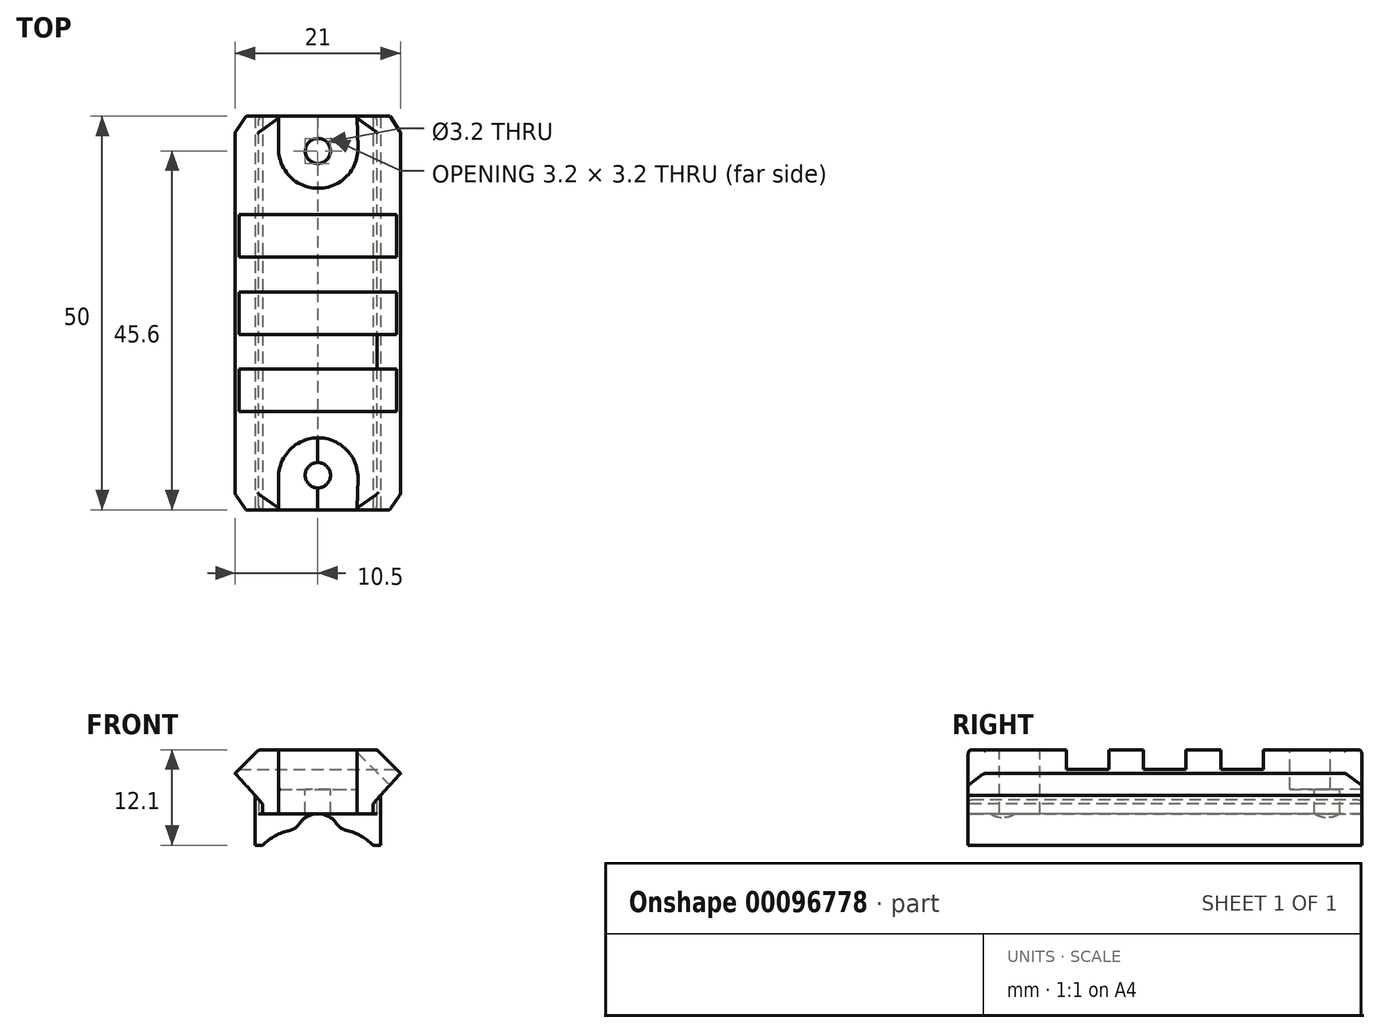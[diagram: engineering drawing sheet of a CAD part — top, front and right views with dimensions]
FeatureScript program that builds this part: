
annotation { "Feature Type Name" : "Feature", "Feature Type Description" : "" }
export const myFeature = defineFeature(function(context is Context, id is Id, definition is map)
    precondition{}
    {
        {
            var Q0;
            Q0=qCreatedBy(makeId("Front.planeOp"),FACE);
            var sketch = newSketch(context, id + "F0", { "sketchPlane" : qUnion([Q0])});
            skPoint(sketch, "E0", {"position": v(7.5, 0) * mm});
            skPoint(sketch, "E1", {"position": v(-7.5, 0) * mm});
            skPoint(sketch, "E2", {"position": v(0, 3.3) * mm});
            skPoint(sketch, "E3", {"position": v(0, -4.8) * mm});
            skLineSegment(sketch, "E4", {"start": v(7.5, -4.8) * mm, "end": v(-7.5, -4.8) * mm});
            skLineSegment(sketch, "E5", {"start": v(7.5, -4.8) * mm, "end": v(7.5, -3) * mm});
            skLineSegment(sketch, "E6", {"start": v(-7.5, -3) * mm, "end": v(-7.5, -4.8) * mm});
            skLineSegment(sketch, "E7", {"start": v(-7.5, -3) * mm, "end": v(-10.5, 0.3) * mm});
            skLineSegment(sketch, "E8", {"start": v(7.5, -3) * mm, "end": v(10.5, 0.3) * mm});
            skPoint(sketch, "E9", {"position": v(7.5, 3.3) * mm});
            skPoint(sketch, "E10", {"position": v(-7.5, 3.3) * mm});
            skLineSegment(sketch, "E11", {"start": v(-10.5, 0.3) * mm, "end": v(-7.5, 3.3) * mm});
            skLineSegment(sketch, "E12", {"start": v(10.5, 0.3) * mm, "end": v(7.5, 3.3) * mm});
            skLineSegment(sketch, "E13", {"start": v(-7.5, 3.3) * mm, "end": v(7.5, 3.3) * mm});
            skSolve(sketch);
        }
        {
            var Q0;
            Q0 = qSketchRegion(id + "F0", true);
            extrude(context, id + "F1", {"entities" : qUnion([Q0]), "endBound" : BoundingType.SYMMETRIC, "depth" : 50 * mm});
        }
        {
            var Q0;
            Q0=makeQuery(id+"F1.opExtrude","SWEPT_FACE",FACE,{"disambiguationData":[OSD([sQuery(id+"F0.wireOp",EDGE,"E13")])]});
            var sketch = newSketch(context, id + "F2", { "sketchPlane" : qUnion([Q0])});
            skPoint(sketch, "E14", {"position": v(0, 2.7) * mm});
            skPoint(sketch, "E15", {"position": v(0, -2.7) * mm});
            skLineSegment(sketch, "E16", {"start": v(-14, -2.7) * mm, "end": v(14, -2.7) * mm});
            skLineSegment(sketch, "E17", {"start": v(14, -2.7) * mm, "end": v(14, 2.7) * mm});
            skLineSegment(sketch, "E18", {"start": v(14, 2.7) * mm, "end": v(-14, 2.7) * mm});
            skLineSegment(sketch, "E19", {"start": v(-14, -2.7) * mm, "end": v(-14, 2.7) * mm});
            skLineSegment(sketch, "E20", {"start": v(0, 25) * mm, "end": v(0, 10) * mm});
            skLineSegment(sketch, "E21.0.1.0", {"start": v(-14, 7.12) * mm, "end": v(-14.1, 12.52) * mm});
            skLineSegment(sketch, "E21.0.1.1", {"start": v(14.12, 12.52) * mm, "end": v(-14.1, 12.52) * mm});
            skLineSegment(sketch, "E21.0.1.2", {"start": v(-14, 7.12) * mm, "end": v(14.12, 7.12) * mm});
            skLineSegment(sketch, "E21.0.1.3", {"start": v(14.12, 7.12) * mm, "end": v(14.12, 12.52) * mm});
            skLineSegment(sketch, "E21.direction2", {"start": v(-14, -2.7) * mm, "end": v(-14, 7.12) * mm, "construction": true});
            skLineSegment(sketch, "E22.0.1.0", {"start": v(-13.9, -12.52) * mm, "end": v(14.62, -12.52) * mm});
            skLineSegment(sketch, "E22.0.1.1", {"start": v(-13.9, -12.52) * mm, "end": v(-13.9, -7.12) * mm});
            skLineSegment(sketch, "E22.0.1.2", {"start": v(14.62, -7.12) * mm, "end": v(-13.9, -7.12) * mm});
            skLineSegment(sketch, "E22.0.1.3", {"start": v(14.62, -12.52) * mm, "end": v(14.62, -7.12) * mm});
            skLineSegment(sketch, "E22.direction2", {"start": v(-14, -2.7) * mm, "end": v(-13.9, -12.52) * mm, "construction": true});
            skLineSegment(sketch, "E23", {"start": v(0, -7.12) * mm, "end": v(0, -12.52) * mm});
            skSolve(sketch);
        }
        {
            var Q0;
            Q0 = qSketchRegion(id + "F2", true);
            extrude(context, id + "F3", {"entities" : qUnion([Q0]), "operationType" : NewBodyOperationType.REMOVE, "oppositeDirection" : true, "depth" : 2.5 * mm});
        }
        {
            var Q0;
            Q0=makeQuery(id+"F1.opExtrude","CAP_EDGE",EDGE,{"disambiguationData":[OSD([sQuery(id+"F0.wireOp",EDGE,"E12")])],"isStart":true});
            var Q1;
            Q1=makeQuery(id+"F1.opExtrude","CAP_EDGE",EDGE,{"disambiguationData":[OSD([sQuery(id+"F0.wireOp",EDGE,"E11")])],"isStart":true});
            var Q2;
            Q2=makeQuery(id+"F1.opExtrude","CAP_EDGE",EDGE,{"disambiguationData":[OSD([sQuery(id+"F0.wireOp",EDGE,"E12")])],"isStart":false});
            var Q3;
            Q3=makeQuery(id+"F1.opExtrude","CAP_EDGE",EDGE,{"disambiguationData":[OSD([sQuery(id+"F0.wireOp",EDGE,"E11")])],"isStart":false});
            chamfer(context, id + "F4", {"entities" : qUnion([Q0, Q1, Q2, Q3]), "width" : 2 * mm, "tangentPropagation" : true});
        }
        {
            var Q0;
            {var subQ0=sQuery(id+"F0.wireOp",EDGE,"E11");var subQ1=sQuery(id+"F0.wireOp",EDGE,"E13");Q0=makeQuery(id+"F3.boolean.opBoolean","SPLIT",EDGE,{"disambiguationData":[TD([makeQuery(id+"F3.opExtrude","SWEPT_FACE",FACE,{"disambiguationData":[OSD([sQuery(id+"F2.wireOp",EDGE,"E21.0.2.1")])]})])],"derivedFrom":makeQuery(id+"F1.opExtrude","SWEPT_EDGE",EDGE,{"disambiguationData":[OSD([subQ0,subQ1])]})});}
            var Q1;
            {var subQ0=sQuery(id+"F0.wireOp",EDGE,"E11");var subQ1=sQuery(id+"F0.wireOp",EDGE,"E13");Q1=makeQuery(id+"F3.boolean.opBoolean","SPLIT",EDGE,{"disambiguationData":[TD([makeQuery(id+"F3.opExtrude","SWEPT_FACE",FACE,{"disambiguationData":[OSD([sQuery(id+"F2.wireOp",EDGE,"E21.0.1.1")])]})])],"derivedFrom":makeQuery(id+"F1.opExtrude","SWEPT_EDGE",EDGE,{"disambiguationData":[OSD([subQ0,subQ1])]})});}
            var Q2;
            {var subQ0=sQuery(id+"F0.wireOp",EDGE,"E11");var subQ1=sQuery(id+"F0.wireOp",EDGE,"E13");Q2=makeQuery(id+"F3.boolean.opBoolean","SPLIT",EDGE,{"disambiguationData":[TD([makeQuery(id+"F3.opExtrude","SWEPT_FACE",FACE,{"disambiguationData":[OSD([sQuery(id+"F2.wireOp",EDGE,"E18")])]})])],"derivedFrom":makeQuery(id+"F1.opExtrude","SWEPT_EDGE",EDGE,{"disambiguationData":[OSD([subQ0,subQ1])]})});}
            var Q3;
            {var subQ0=sQuery(id+"F0.wireOp",EDGE,"E11");var subQ1=sQuery(id+"F0.wireOp",EDGE,"E13");Q3=makeQuery(id+"F3.boolean.opBoolean","SPLIT",EDGE,{"disambiguationData":[TD([makeQuery(id+"F3.opExtrude","SWEPT_FACE",FACE,{"disambiguationData":[OSD([sQuery(id+"F2.wireOp",EDGE,"E16")])]})])],"derivedFrom":makeQuery(id+"F1.opExtrude","SWEPT_EDGE",EDGE,{"disambiguationData":[OSD([subQ0,subQ1])]})});}
            var Q4;
            {var subQ0=sQuery(id+"F0.wireOp",EDGE,"E11");var subQ1=sQuery(id+"F0.wireOp",EDGE,"E13");Q4=makeQuery(id+"F3.boolean.opBoolean","SPLIT",EDGE,{"disambiguationData":[TD([makeQuery(id+"F3.opExtrude","SWEPT_FACE",FACE,{"disambiguationData":[OSD([sQuery(id+"F2.wireOp",EDGE,"E22.0.1.0")])]})])],"derivedFrom":makeQuery(id+"F1.opExtrude","SWEPT_EDGE",EDGE,{"disambiguationData":[OSD([subQ0,subQ1])]})});}
            var Q5;
            {var subQ0=sQuery(id+"F0.wireOp",EDGE,"E11");var subQ1=sQuery(id+"F0.wireOp",EDGE,"E13");Q5=makeQuery(id+"F3.boolean.opBoolean","SPLIT",EDGE,{"disambiguationData":[TD([makeQuery(id+"F3.opExtrude","SWEPT_FACE",FACE,{"disambiguationData":[OSD([sQuery(id+"F2.wireOp",EDGE,"E22.0.2.0")])]})])],"derivedFrom":makeQuery(id+"F1.opExtrude","SWEPT_EDGE",EDGE,{"disambiguationData":[OSD([subQ0,subQ1])]})});}
            var Q6;
            {var subQ0=sQuery(id+"F0.wireOp",EDGE,"E12");var subQ1=sQuery(id+"F0.wireOp",EDGE,"E13");Q6=makeQuery(id+"F3.boolean.opBoolean","SPLIT",EDGE,{"disambiguationData":[TD([makeQuery(id+"F3.opExtrude","SWEPT_FACE",FACE,{"disambiguationData":[OSD([sQuery(id+"F2.wireOp",EDGE,"E22.0.2.0")])]})])],"derivedFrom":makeQuery(id+"F1.opExtrude","SWEPT_EDGE",EDGE,{"disambiguationData":[OSD([subQ0,subQ1])]})});}
            var Q7;
            {var subQ0=sQuery(id+"F0.wireOp",EDGE,"E12");var subQ1=sQuery(id+"F0.wireOp",EDGE,"E13");Q7=makeQuery(id+"F3.boolean.opBoolean","SPLIT",EDGE,{"disambiguationData":[TD([makeQuery(id+"F3.opExtrude","SWEPT_FACE",FACE,{"disambiguationData":[OSD([sQuery(id+"F2.wireOp",EDGE,"E22.0.1.0")])]})])],"derivedFrom":makeQuery(id+"F1.opExtrude","SWEPT_EDGE",EDGE,{"disambiguationData":[OSD([subQ0,subQ1])]})});}
            var Q8;
            {var subQ0=sQuery(id+"F0.wireOp",EDGE,"E12");var subQ1=sQuery(id+"F0.wireOp",EDGE,"E13");Q8=makeQuery(id+"F3.boolean.opBoolean","SPLIT",EDGE,{"disambiguationData":[TD([makeQuery(id+"F3.opExtrude","SWEPT_FACE",FACE,{"disambiguationData":[OSD([sQuery(id+"F2.wireOp",EDGE,"E18")])]})])],"derivedFrom":makeQuery(id+"F1.opExtrude","SWEPT_EDGE",EDGE,{"disambiguationData":[OSD([subQ0,subQ1])]})});}
            var Q9;
            {var subQ0=sQuery(id+"F0.wireOp",EDGE,"E12");var subQ1=sQuery(id+"F0.wireOp",EDGE,"E13");Q9=makeQuery(id+"F3.boolean.opBoolean","SPLIT",EDGE,{"disambiguationData":[TD([makeQuery(id+"F3.opExtrude","SWEPT_FACE",FACE,{"disambiguationData":[OSD([sQuery(id+"F2.wireOp",EDGE,"E21.0.1.1")])]})])],"derivedFrom":makeQuery(id+"F1.opExtrude","SWEPT_EDGE",EDGE,{"disambiguationData":[OSD([subQ0,subQ1])]})});}
            var Q10;
            {var subQ0=sQuery(id+"F0.wireOp",EDGE,"E12");var subQ1=sQuery(id+"F0.wireOp",EDGE,"E13");Q10=makeQuery(id+"F3.boolean.opBoolean","SPLIT",EDGE,{"disambiguationData":[TD([makeQuery(id+"F3.opExtrude","SWEPT_FACE",FACE,{"disambiguationData":[OSD([sQuery(id+"F2.wireOp",EDGE,"E21.0.2.1")])]})])],"derivedFrom":makeQuery(id+"F1.opExtrude","SWEPT_EDGE",EDGE,{"disambiguationData":[OSD([subQ0,subQ1])]})});}
            var Q11;
            {var subQ0=sQuery(id+"F0.wireOp",EDGE,"E13");var subQ2=sQuery(id+"F0.wireOp",EDGE,"E11");Q11=makeQuery(id+"F4.opChamfer","BLEND_EDGE",EDGE,{"blendedFrom":[makeQuery(id+"F1.opExtrude","CAP_EDGE",EDGE,{"disambiguationData":[OSD([subQ2])],"isStart":true}),makeQuery(id+"F3.boolean.opBoolean","SPLIT",FACE,{"disambiguationData":[TD([makeQuery(id+"F3.opExtrude","SWEPT_FACE",FACE,{"disambiguationData":[OSD([sQuery(id+"F2.wireOp",EDGE,"E21.0.3.1")])]})])],"derivedFrom":makeQuery(id+"F1.opExtrude","SWEPT_FACE",FACE,{"disambiguationData":[OSD([subQ0])]})})],"blendedInto":[makeQuery(id+"F3.boolean.opBoolean","SPLIT",FACE,{"disambiguationData":[TD([makeQuery(id+"F3.opExtrude","SWEPT_FACE",FACE,{"disambiguationData":[OSD([sQuery(id+"F2.wireOp",EDGE,"E21.0.3.1")])]})])],"derivedFrom":makeQuery(id+"F1.opExtrude","SWEPT_FACE",FACE,{"disambiguationData":[OSD([subQ0])]})})]});}
            var Q12;
            {var subQ0=sQuery(id+"F0.wireOp",EDGE,"E11");Q12=makeQuery(id+"F4.opChamfer","BLEND_EDGE",EDGE,{"blendedFrom":[makeQuery(id+"F1.opExtrude","CAP_EDGE",EDGE,{"disambiguationData":[OSD([subQ0])],"isStart":true}),makeQuery(id+"F1.opExtrude","CAP_FACE",FACE,{"disambiguationData":[OSD([sQuery(id+"F0.wireOp",EDGE,"E4"),sQuery(id+"F0.wireOp",EDGE,"E5"),sQuery(id+"F0.wireOp",EDGE,"E6"),sQuery(id+"F0.wireOp",EDGE,"E7"),sQuery(id+"F0.wireOp",EDGE,"E8"),subQ0,sQuery(id+"F0.wireOp",EDGE,"E12"),sQuery(id+"F0.wireOp",EDGE,"E13")])],"isStart":true})],"blendedInto":[makeQuery(id+"F1.opExtrude","CAP_FACE",FACE,{"disambiguationData":[OSD([sQuery(id+"F0.wireOp",EDGE,"E4"),sQuery(id+"F0.wireOp",EDGE,"E5"),sQuery(id+"F0.wireOp",EDGE,"E6"),sQuery(id+"F0.wireOp",EDGE,"E7"),sQuery(id+"F0.wireOp",EDGE,"E8"),subQ0,sQuery(id+"F0.wireOp",EDGE,"E12"),sQuery(id+"F0.wireOp",EDGE,"E13")])],"isStart":true})]});}
            var Q13;
            {var subQ0=sQuery(id+"F0.wireOp",EDGE,"E13");var subQ1=sQuery(id+"F0.wireOp",EDGE,"E12");Q13=makeQuery(id+"F4.opChamfer","BLEND_EDGE",EDGE,{"blendedFrom":[makeQuery(id+"F1.opExtrude","CAP_EDGE",EDGE,{"disambiguationData":[OSD([subQ1])],"isStart":true}),makeQuery(id+"F3.boolean.opBoolean","SPLIT",FACE,{"disambiguationData":[TD([makeQuery(id+"F3.opExtrude","SWEPT_FACE",FACE,{"disambiguationData":[OSD([sQuery(id+"F2.wireOp",EDGE,"E21.0.3.1")])]})])],"derivedFrom":makeQuery(id+"F1.opExtrude","SWEPT_FACE",FACE,{"disambiguationData":[OSD([subQ0])]})})],"blendedInto":[makeQuery(id+"F3.boolean.opBoolean","SPLIT",FACE,{"disambiguationData":[TD([makeQuery(id+"F3.opExtrude","SWEPT_FACE",FACE,{"disambiguationData":[OSD([sQuery(id+"F2.wireOp",EDGE,"E21.0.3.1")])]})])],"derivedFrom":makeQuery(id+"F1.opExtrude","SWEPT_FACE",FACE,{"disambiguationData":[OSD([subQ0])]})})]});}
            var Q14;
            {var subQ0=sQuery(id+"F0.wireOp",EDGE,"E12");Q14=makeQuery(id+"F4.opChamfer","BLEND_EDGE",EDGE,{"blendedFrom":[makeQuery(id+"F1.opExtrude","CAP_EDGE",EDGE,{"disambiguationData":[OSD([subQ0])],"isStart":true}),makeQuery(id+"F1.opExtrude","SWEPT_FACE",FACE,{"disambiguationData":[OSD([subQ0])]})],"blendedInto":[makeQuery(id+"F1.opExtrude","SWEPT_FACE",FACE,{"disambiguationData":[OSD([subQ0])]})]});}
            var Q15;
            {var subQ0=sQuery(id+"F0.wireOp",EDGE,"E11");Q15=makeQuery(id+"F4.opChamfer","BLEND_EDGE",EDGE,{"blendedFrom":[makeQuery(id+"F1.opExtrude","CAP_EDGE",EDGE,{"disambiguationData":[OSD([subQ0])],"isStart":true}),makeQuery(id+"F1.opExtrude","SWEPT_FACE",FACE,{"disambiguationData":[OSD([subQ0])]})],"blendedInto":[makeQuery(id+"F1.opExtrude","SWEPT_FACE",FACE,{"disambiguationData":[OSD([subQ0])]})]});}
            var Q16;
            {var subQ0=sQuery(id+"F0.wireOp",EDGE,"E12");Q16=makeQuery(id+"F4.opChamfer","BLEND_EDGE",EDGE,{"blendedFrom":[makeQuery(id+"F1.opExtrude","CAP_EDGE",EDGE,{"disambiguationData":[OSD([subQ0])],"isStart":false}),makeQuery(id+"F1.opExtrude","CAP_FACE",FACE,{"disambiguationData":[OSD([sQuery(id+"F0.wireOp",EDGE,"E4"),sQuery(id+"F0.wireOp",EDGE,"E5"),sQuery(id+"F0.wireOp",EDGE,"E6"),sQuery(id+"F0.wireOp",EDGE,"E7"),sQuery(id+"F0.wireOp",EDGE,"E8"),sQuery(id+"F0.wireOp",EDGE,"E11"),subQ0,sQuery(id+"F0.wireOp",EDGE,"E13")])],"isStart":false})],"blendedInto":[makeQuery(id+"F1.opExtrude","CAP_FACE",FACE,{"disambiguationData":[OSD([sQuery(id+"F0.wireOp",EDGE,"E4"),sQuery(id+"F0.wireOp",EDGE,"E5"),sQuery(id+"F0.wireOp",EDGE,"E6"),sQuery(id+"F0.wireOp",EDGE,"E7"),sQuery(id+"F0.wireOp",EDGE,"E8"),sQuery(id+"F0.wireOp",EDGE,"E11"),subQ0,sQuery(id+"F0.wireOp",EDGE,"E13")])],"isStart":false})]});}
            var Q17;
            {var subQ0=sQuery(id+"F0.wireOp",EDGE,"E12");Q17=makeQuery(id+"F4.opChamfer","BLEND_EDGE",EDGE,{"blendedFrom":[makeQuery(id+"F1.opExtrude","CAP_EDGE",EDGE,{"disambiguationData":[OSD([subQ0])],"isStart":false}),makeQuery(id+"F1.opExtrude","SWEPT_FACE",FACE,{"disambiguationData":[OSD([subQ0])]})],"blendedInto":[makeQuery(id+"F1.opExtrude","SWEPT_FACE",FACE,{"disambiguationData":[OSD([subQ0])]})]});}
            var Q18;
            {var subQ0=sQuery(id+"F0.wireOp",EDGE,"E13");var subQ1=sQuery(id+"F0.wireOp",EDGE,"E12");Q18=makeQuery(id+"F4.opChamfer","BLEND_EDGE",EDGE,{"blendedFrom":[makeQuery(id+"F1.opExtrude","CAP_EDGE",EDGE,{"disambiguationData":[OSD([subQ1])],"isStart":false}),makeQuery(id+"F3.boolean.opBoolean","SPLIT",FACE,{"disambiguationData":[TD([makeQuery(id+"F3.opExtrude","SWEPT_FACE",FACE,{"disambiguationData":[OSD([sQuery(id+"F2.wireOp",EDGE,"E22.0.3.0")])]})])],"derivedFrom":makeQuery(id+"F1.opExtrude","SWEPT_FACE",FACE,{"disambiguationData":[OSD([subQ0])]})})],"blendedInto":[makeQuery(id+"F3.boolean.opBoolean","SPLIT",FACE,{"disambiguationData":[TD([makeQuery(id+"F3.opExtrude","SWEPT_FACE",FACE,{"disambiguationData":[OSD([sQuery(id+"F2.wireOp",EDGE,"E22.0.3.0")])]})])],"derivedFrom":makeQuery(id+"F1.opExtrude","SWEPT_FACE",FACE,{"disambiguationData":[OSD([subQ0])]})})]});}
            var Q19;
            {var subQ0=sQuery(id+"F0.wireOp",EDGE,"E11");Q19=makeQuery(id+"F4.opChamfer","BLEND_EDGE",EDGE,{"blendedFrom":[makeQuery(id+"F1.opExtrude","CAP_EDGE",EDGE,{"disambiguationData":[OSD([subQ0])],"isStart":false}),makeQuery(id+"F1.opExtrude","CAP_FACE",FACE,{"disambiguationData":[OSD([sQuery(id+"F0.wireOp",EDGE,"E4"),sQuery(id+"F0.wireOp",EDGE,"E5"),sQuery(id+"F0.wireOp",EDGE,"E6"),sQuery(id+"F0.wireOp",EDGE,"E7"),sQuery(id+"F0.wireOp",EDGE,"E8"),subQ0,sQuery(id+"F0.wireOp",EDGE,"E12"),sQuery(id+"F0.wireOp",EDGE,"E13")])],"isStart":false})],"blendedInto":[makeQuery(id+"F1.opExtrude","CAP_FACE",FACE,{"disambiguationData":[OSD([sQuery(id+"F0.wireOp",EDGE,"E4"),sQuery(id+"F0.wireOp",EDGE,"E5"),sQuery(id+"F0.wireOp",EDGE,"E6"),sQuery(id+"F0.wireOp",EDGE,"E7"),sQuery(id+"F0.wireOp",EDGE,"E8"),subQ0,sQuery(id+"F0.wireOp",EDGE,"E12"),sQuery(id+"F0.wireOp",EDGE,"E13")])],"isStart":false})]});}
            var Q20;
            {var subQ0=sQuery(id+"F0.wireOp",EDGE,"E13");var subQ2=sQuery(id+"F0.wireOp",EDGE,"E11");Q20=makeQuery(id+"F4.opChamfer","BLEND_EDGE",EDGE,{"blendedFrom":[makeQuery(id+"F1.opExtrude","CAP_EDGE",EDGE,{"disambiguationData":[OSD([subQ2])],"isStart":false}),makeQuery(id+"F3.boolean.opBoolean","SPLIT",FACE,{"disambiguationData":[TD([makeQuery(id+"F3.opExtrude","SWEPT_FACE",FACE,{"disambiguationData":[OSD([sQuery(id+"F2.wireOp",EDGE,"E22.0.3.0")])]})])],"derivedFrom":makeQuery(id+"F1.opExtrude","SWEPT_FACE",FACE,{"disambiguationData":[OSD([subQ0])]})})],"blendedInto":[makeQuery(id+"F3.boolean.opBoolean","SPLIT",FACE,{"disambiguationData":[TD([makeQuery(id+"F3.opExtrude","SWEPT_FACE",FACE,{"disambiguationData":[OSD([sQuery(id+"F2.wireOp",EDGE,"E22.0.3.0")])]})])],"derivedFrom":makeQuery(id+"F1.opExtrude","SWEPT_FACE",FACE,{"disambiguationData":[OSD([subQ0])]})})]});}
            var Q21;
            {var subQ0=sQuery(id+"F0.wireOp",EDGE,"E11");Q21=makeQuery(id+"F4.opChamfer","BLEND_EDGE",EDGE,{"blendedFrom":[makeQuery(id+"F1.opExtrude","CAP_EDGE",EDGE,{"disambiguationData":[OSD([subQ0])],"isStart":false}),makeQuery(id+"F1.opExtrude","SWEPT_FACE",FACE,{"disambiguationData":[OSD([subQ0])]})],"blendedInto":[makeQuery(id+"F1.opExtrude","SWEPT_FACE",FACE,{"disambiguationData":[OSD([subQ0])]})]});}
            var Q22;
            Q22=makeQuery(id+"F1.opExtrude","CAP_EDGE",EDGE,{"disambiguationData":[OSD([sQuery(id+"F0.wireOp",EDGE,"E6")])],"isStart":false});
            var Q23;
            Q23=makeQuery(id+"F1.opExtrude","CAP_EDGE",EDGE,{"disambiguationData":[OSD([sQuery(id+"F0.wireOp",EDGE,"E5")])],"isStart":false});
            var Q24;
            Q24=makeQuery(id+"F1.opExtrude","CAP_EDGE",EDGE,{"disambiguationData":[OSD([sQuery(id+"F0.wireOp",EDGE,"E5")])],"isStart":true});
            var Q25;
            Q25=makeQuery(id+"F1.opExtrude","CAP_EDGE",EDGE,{"disambiguationData":[OSD([sQuery(id+"F0.wireOp",EDGE,"E6")])],"isStart":true});
            fillet(context, id + "F5", {"entities" : qUnion([Q0, Q1, Q2, Q3, Q4, Q5, Q6, Q7, Q8, Q9, Q10, Q11, Q12, Q13, Q14, Q15, Q16, Q17, Q18, Q19, Q20, Q21, Q22, Q23, Q24, Q25]), "radius" : 0.5 * mm, "tangentPropagation" : true, "allowEdgeOverflow" : false});
        }
        {
            var Q0;
            Q0=qCreatedBy(makeId("Right.planeOp"),FACE);
            var sketch = newSketch(context, id + "F6", { "sketchPlane" : qUnion([Q0])});
            skLineSegment(sketch, "E24.bottom", {"start": v(-60.58, 29.92) * mm, "end": v(-11.98, 29.92) * mm});
            skLineSegment(sketch, "E24.top", {"start": v(-60.58, -17.9) * mm, "end": v(-11.98, -17.9) * mm});
            skLineSegment(sketch, "E24.left", {"start": v(-60.58, 29.92) * mm, "end": v(-60.58, -17.9) * mm});
            skLineSegment(sketch, "E24.right", {"start": v(-11.98, 29.92) * mm, "end": v(-11.98, -17.9) * mm});
            skLineSegment(sketch, "E25.bottom", {"start": v(57.87, 29.92) * mm, "end": v(11.63, 29.92) * mm});
            skLineSegment(sketch, "E25.top", {"start": v(57.87, -22.23) * mm, "end": v(11.63, -22.23) * mm});
            skLineSegment(sketch, "E25.left", {"start": v(57.87, 29.92) * mm, "end": v(57.87, -22.23) * mm});
            skLineSegment(sketch, "E25.right", {"start": v(11.63, 29.92) * mm, "end": v(11.63, -22.23) * mm});
            skSolve(sketch);
        }
        {
            var Q0;
            {var subQ0=sQuery(id+"F0.wireOp",EDGE,"E13");Q0=makeQuery(id+"F3.boolean.opBoolean","SPLIT",FACE,{"disambiguationData":[TD([makeQuery(id+"F3.opExtrude","SWEPT_FACE",FACE,{"disambiguationData":[OSD([sQuery(id+"F2.wireOp",EDGE,"E22.0.1.0")])]})])],"derivedFrom":makeQuery(id+"F1.opExtrude","SWEPT_FACE",FACE,{"disambiguationData":[OSD([subQ0])]})});}
            var sketch = newSketch(context, id + "F7", { "sketchPlane" : qUnion([Q0])});
            skLineSegment(sketch, "E26", {"start": v(0, -25) * mm, "end": v(5, -25) * mm});
            skLineSegment(sketch, "E27", {"start": v(5, -25) * mm, "end": v(5.09, -21) * mm});
            skPoint(sketch, "E27.endSnap0", {"position": v(5.09, -24.5) * mm});
            skLineSegment(sketch, "E28", {"start": v(0, -25) * mm, "end": v(0, -21) * mm});
            skLineSegment(sketch, "E29", {"start": v(0, -25) * mm, "end": v(-5, -25) * mm});
            skLineSegment(sketch, "E30", {"start": v(-5, -25) * mm, "end": v(-5, -21) * mm});
            skArc(sketch, "E31", {"start": v(5.09, -21) * mm, "mid": v(0.04, -15.85) * mm, "end": v(-5, -21) * mm});
            skLineSegment(sketch, "E32", {"start": v(16.52, 0) * mm, "end": v(-28.74, 0) * mm});
            skArc(sketch, "E33.MirrorCS", {"start": v(5.09, 21) * mm, "mid": v(0.04, 15.85) * mm, "end": v(-5, 21) * mm});
            skLineSegment(sketch, "E34.MirrorCS", {"start": v(5, 25) * mm, "end": v(5.09, 21) * mm});
            skLineSegment(sketch, "E35.MirrorCS", {"start": v(-5, 25) * mm, "end": v(-5, 21) * mm});
            skLineSegment(sketch, "E36", {"start": v(-5, 25) * mm, "end": v(5, 25) * mm});
            skLineSegment(sketch, "E37", {"start": v(-5, -25) * mm, "end": v(5, -25) * mm});
            skSolve(sketch);
        }
        {
            var Q0;
            Q0 = qSketchRegion(id + "F7", true);
            extrude(context, id + "F8", {"entities" : qUnion([Q0]), "operationType" : NewBodyOperationType.REMOVE, "oppositeDirection" : true, "depth" : 5 * mm});
        }
        {
            var Q0;
            Q0=makeQuery(id+"F8.boolean.opBoolean","COPY",FACE,{"derivedFrom":makeQuery(id+"F8.opExtrude","CAP_FACE",FACE,{"disambiguationData":[OSD([sQuery(id+"F7.wireOp",EDGE,"E33.MirrorCS"),sQuery(id+"F7.wireOp",EDGE,"E34.MirrorCS"),sQuery(id+"F7.wireOp",EDGE,"E35.MirrorCS"),sQuery(id+"F7.wireOp",EDGE,"E36")])],"isStart":false})});
            var sketch = newSketch(context, id + "F9", { "sketchPlane" : qUnion([Q0])});
            skCircle(sketch, "E38", {"center": v(0, 20.6) * mm, "radius": 1.6 * mm});
            skLineSegment(sketch, "E39", {"start": v(-5, 25) * mm, "end": v(-5, 21) * mm});
            skLineSegment(sketch, "E40", {"start": v(5, 25) * mm, "end": v(5.09, 21) * mm});
            skArc(sketch, "E41", {"start": v(-5, 21) * mm, "mid": v(0.04, 15.85) * mm, "end": v(5.09, 21) * mm});
            skLineSegment(sketch, "E42", {"start": v(-5, 25) * mm, "end": v(5, 25) * mm});
            skLineSegment(sketch, "E43", {"start": v(-17.18, 0) * mm, "end": v(17.6, 0) * mm});
            skCircle(sketch, "E44.MirrorC", {"center": v(0, -20.6) * mm, "radius": 1.6 * mm});
            skLineSegment(sketch, "E45.MirrorCS", {"start": v(-5, -25) * mm, "end": v(5, -25) * mm});
            skArc(sketch, "E46.MirrorCS", {"start": v(-5, -21) * mm, "mid": v(0.04, -15.85) * mm, "end": v(5.09, -21) * mm});
            skLineSegment(sketch, "E47.MirrorCS", {"start": v(-5, -25) * mm, "end": v(-5, -21) * mm});
            skLineSegment(sketch, "E48.MirrorCS", {"start": v(5, -25) * mm, "end": v(5.09, -21) * mm});
            skSolve(sketch);
        }
        {
            var Q0;
            Q0=makeQuery(id+"F9.imprint","IMPRINT",FACE,{"disambiguationData":[TD([[makeQuery(id+"F9.imprint","IMPRINT",EDGE,{"derivedFrom":sQuery(id+"F9.wireOp",EDGE,"E44.MirrorC")}),-1.0]])]});
            var Q1;
            Q1=makeQuery(id+"F9.imprint","IMPRINT",FACE,{"disambiguationData":[TD([[makeQuery(id+"F9.imprint","IMPRINT",EDGE,{"derivedFrom":sQuery(id+"F9.wireOp",EDGE,"E38")}),1.0]])]});
            extrude(context, id + "F10", {"entities" : qUnion([Q0, Q1]), "operationType" : NewBodyOperationType.REMOVE, "endBound" : BoundingType.THROUGH_ALL, "oppositeDirection" : true, "depth" : 25 * mm});
        }
        {
            var Q0;
            Q0=makeQuery(id+"F1.opExtrude","CAP_FACE",FACE,{"disambiguationData":[OSD([sQuery(id+"F0.wireOp",EDGE,"E4"),sQuery(id+"F0.wireOp",EDGE,"E5"),sQuery(id+"F0.wireOp",EDGE,"E6"),sQuery(id+"F0.wireOp",EDGE,"E7"),sQuery(id+"F0.wireOp",EDGE,"E8"),sQuery(id+"F0.wireOp",EDGE,"E11"),sQuery(id+"F0.wireOp",EDGE,"E12"),sQuery(id+"F0.wireOp",EDGE,"E13")])],"isStart":false});
            var sketch = newSketch(context, id + "F11", { "sketchPlane" : qUnion([Q0])});
            skLineSegment(sketch, "E49", {"start": v(0, -4.8) * mm, "end": v(2.5, -4.8) * mm});
            skLineSegment(sketch, "E50", {"start": v(0, -4.8) * mm, "end": v(-2.5, -4.8) * mm});
            skArc(sketch, "E51", {"start": v(2.72, -6.78) * mm, "mid": v(1.68, -5.35) * mm, "end": v(0, -4.8) * mm});
            skArc(sketch, "E52", {"start": v(0, -4.8) * mm, "mid": v(-1.64, -5.34) * mm, "end": v(-2.64, -6.75) * mm});
            skLineSegment(sketch, "E53", {"start": v(-7, -4.8) * mm, "end": v(-2.5, -4.8) * mm});
            skLineSegment(sketch, "E54", {"start": v(2.5, -4.8) * mm, "end": v(7, -4.8) * mm});
            skArc(sketch, "E55", {"start": v(-2.64, -6.75) * mm, "mid": v(-5, -7.39) * mm, "end": v(-7, -8.8) * mm});
            skArc(sketch, "E56", {"start": v(7, -8.8) * mm, "mid": v(5.05, -7.4) * mm, "end": v(2.72, -6.78) * mm});
            skLineSegment(sketch, "E57", {"start": v(7, -8.8) * mm, "end": v(8, -8.8) * mm});
            skLineSegment(sketch, "E58", {"start": v(-7, -8.8) * mm, "end": v(-8, -8.8) * mm});
            skLineSegment(sketch, "E59", {"start": v(8, -8.8) * mm, "end": v(8, -2.45) * mm});
            skLineSegment(sketch, "E60", {"start": v(8, -2.45) * mm, "end": v(7, -3.55) * mm});
            skLineSegment(sketch, "E61", {"start": v(7, -3.55) * mm, "end": v(7, -4.8) * mm});
            skLineSegment(sketch, "E62", {"start": v(-8, -8.8) * mm, "end": v(-8, -2.45) * mm});
            skLineSegment(sketch, "E63", {"start": v(-8, -2.45) * mm, "end": v(-7, -3.55) * mm});
            skLineSegment(sketch, "E64", {"start": v(-7, -3.55) * mm, "end": v(-7, -4.8) * mm});
            skSolve(sketch);
        }
        {
            var Q0;
            Q0 = qSketchRegion(id + "F11", true);
            var Q1;
            Q1=makeQuery(id+"F11.imprint","IMPRINT",FACE,{"disambiguationData":[TD([[makeQuery(id+"F11.imprint","IMPRINT",EDGE,{"derivedFrom":sQuery(id+"F11.wireOp",EDGE,"E50")}),1.0]])]});
            extrude(context, id + "F12", {"entities" : qUnion([Q0, Q1]), "oppositeDirection" : true, "depth" : 50 * mm});
        }
        {
            var Q0;
            Q0=makeQuery(id+"F12.opExtrude","SWEPT_EDGE",EDGE,{"disambiguationData":[OSD([sQuery(id+"F11.wireOp",EDGE,"E52"),sQuery(id+"F11.wireOp",EDGE,"E55")])]});
            fillet(context, id + "F14", {"entities" : qUnion([Q0]), "radius" : 2 * mm, "tangentPropagation" : true, "allowEdgeOverflow" : false});
        }
        {
            var Q0;
            Q0=makeQuery(id+"F12.opExtrude","SWEPT_EDGE",EDGE,{"disambiguationData":[OSD([sQuery(id+"F11.wireOp",EDGE,"E51"),sQuery(id+"F11.wireOp",EDGE,"E56")])]});
            fillet(context, id + "F15", {"entities" : qUnion([Q0]), "radius" : 2 * mm, "tangentPropagation" : true, "allowEdgeOverflow" : false});
        }
        {
            var Q0;
            Q0=qCreatedBy(makeId("Top.planeOp"),FACE);
            cPlane(context, id + "F16", {"entities" : qUnion([Q0]), "cplaneType" : CPlaneType.OFFSET, "offset" : 25 * mm, "width" : 150 * mm, "height" : 150 * mm});
        }
        {
            var Q0;
            Q0=qCreatedBy(id+"F16.planeOp",FACE);
            var sketch = newSketch(context, id + "F17", { "sketchPlane" : qUnion([Q0])});
            skCircle(sketch, "E65", {"center": v(0, 20.6) * mm, "radius": 1.6 * mm});
            skCircle(sketch, "E66", {"center": v(0, -20.6) * mm, "radius": 1.6 * mm});
            skSolve(sketch);
        }
        {
            var Q0;
            Q0 = qSketchRegion(id + "F17", true);
            extrude(context, id + "F18", {"entities" : qUnion([Q0]), "operationType" : NewBodyOperationType.REMOVE, "oppositeDirection" : true, "depth" : 47.9 * mm});
        }
    });
